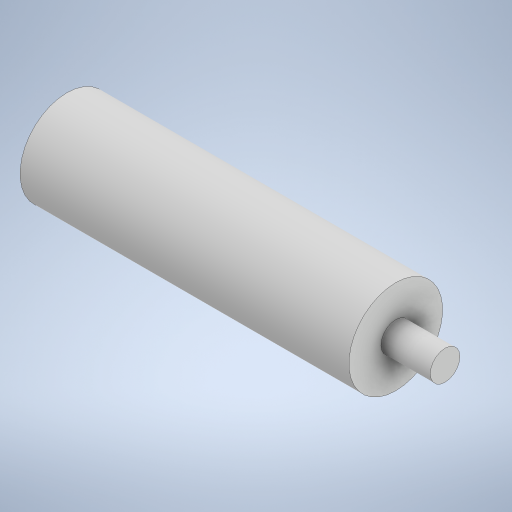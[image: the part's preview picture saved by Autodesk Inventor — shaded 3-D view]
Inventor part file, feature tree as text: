
AUTODESK INVENTOR PART (.ipt)
format: ipt  version: 2023 (Build 270158000, 158)  size: 232,448 bytes
history: native  units: mm
features: extrude x2, sketch x2
ambient origin geometry x8: Origin, YZ Plane, XZ Plane, XY Plane, X Axis, Y Axis, Z Axis, Center Point
bodies: Solid1 (feature_tree)
feature tree (4):
  extrude  "Extrusion1"  Depth=20.0mm TaperAngle=0.0deg
  extrude  "Extrusion2"  Depth=3.0mm TaperAngle=0.0deg
  sketch  "Sketch1"  dims[d0=5.7mm d1=20.0mm d2=0.0mm]
  sketch  "Sketch2"  dims[d3=1.8mm d4=3.0mm d5=0.0mm]
